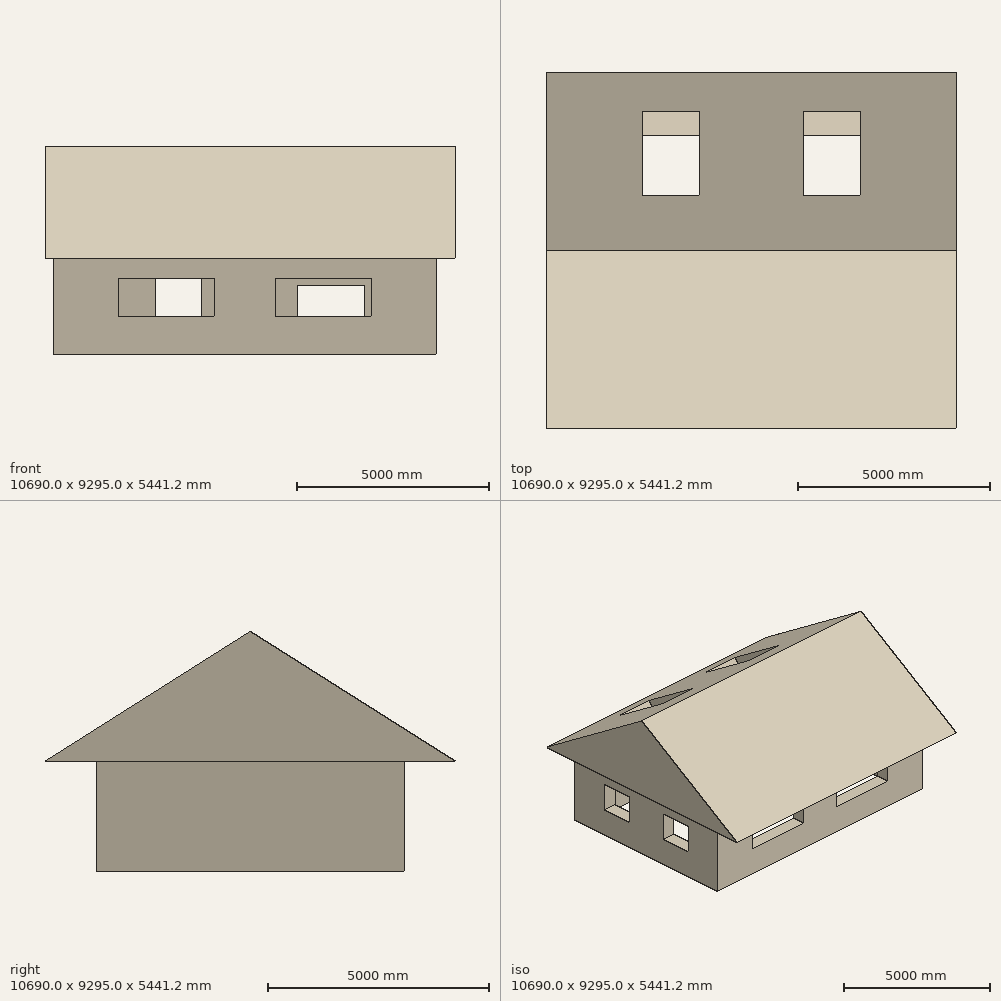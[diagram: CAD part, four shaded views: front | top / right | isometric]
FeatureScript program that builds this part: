
annotation { "Feature Type Name" : "Feature", "Feature Type Description" : "" }
export const myFeature = defineFeature(function(context is Context, id is Id, definition is map)
    precondition{}
    {
        {
            var Q0;
            Q0=qCreatedBy(makeId("Top.planeOp"),FACE);
            var sketch = newSketch(context, id + "F0", { "sketchPlane" : qUnion([Q0])});
            skLineSegment(sketch, "E0.bottom", {"start": v(-4999.87, 2448.69) * mm, "end": v(5000.13, 2448.69) * mm});
            skLineSegment(sketch, "E0.top", {"start": v(-4999.87, -4551.31) * mm, "end": v(5000.13, -4551.31) * mm});
            skLineSegment(sketch, "E0.left", {"start": v(-4999.87, 2448.69) * mm, "end": v(-4999.87, -4551.31) * mm});
            skLineSegment(sketch, "E0.right", {"start": v(5000.13, 2448.69) * mm, "end": v(5000.13, -4551.31) * mm});
            skLineSegment(sketch, "E1.bottom", {"start": v(-4499.87, 1948.69) * mm, "end": v(4500.13, 1948.69) * mm});
            skLineSegment(sketch, "E1.top", {"start": v(-4499.87, -4051.31) * mm, "end": v(4500.13, -4051.31) * mm});
            skLineSegment(sketch, "E1.left", {"start": v(-4499.87, 1948.69) * mm, "end": v(-4499.87, -4051.31) * mm});
            skLineSegment(sketch, "E1.right", {"start": v(4500.13, 1948.69) * mm, "end": v(4500.13, -4051.31) * mm});
            skLineSegment(sketch, "E2.0", {"start": v(-4999.87, 2443.69) * mm, "end": v(5000.13, 2443.69) * mm});
            skLineSegment(sketch, "E3.bottom", {"start": v(-2859.87, 2443.69) * mm, "end": v(-1609.87, 2443.69) * mm});
            skLineSegment(sketch, "E3.top", {"start": v(-2859.87, 1948.69) * mm, "end": v(-1609.87, 1948.69) * mm});
            skLineSegment(sketch, "E3.left", {"start": v(-2859.87, 2443.69) * mm, "end": v(-2859.87, 1948.69) * mm});
            skLineSegment(sketch, "E3.right", {"start": v(-1609.87, 2443.69) * mm, "end": v(-1609.87, 1948.69) * mm});
            skLineSegment(sketch, "E4.bottom", {"start": v(1610.13, 2443.69) * mm, "end": v(2860.13, 2443.69) * mm});
            skLineSegment(sketch, "E4.top", {"start": v(1610.13, 1948.69) * mm, "end": v(2860.13, 1948.69) * mm});
            skLineSegment(sketch, "E4.left", {"start": v(1610.13, 2443.69) * mm, "end": v(1610.13, 1948.69) * mm});
            skLineSegment(sketch, "E4.right", {"start": v(2860.13, 2443.69) * mm, "end": v(2860.13, 1948.69) * mm});
            skLineSegment(sketch, "E5.bottom", {"start": v(4500.13, 198.69) * mm, "end": v(5000.13, 198.69) * mm});
            skLineSegment(sketch, "E5.top", {"start": v(4500.13, -1051.31) * mm, "end": v(5000.13, -1051.31) * mm});
            skLineSegment(sketch, "E5.left", {"start": v(4500.13, 198.69) * mm, "end": v(4500.13, -1051.31) * mm});
            skLineSegment(sketch, "E5.right", {"start": v(5000.13, 198.69) * mm, "end": v(5000.13, -1051.31) * mm});
            skLineSegment(sketch, "E6.bottom", {"start": v(4500.13, -2032.66) * mm, "end": v(5000.13, -2032.66) * mm});
            skLineSegment(sketch, "E6.top", {"start": v(4500.13, -3239.36) * mm, "end": v(5000.13, -3239.36) * mm});
            skLineSegment(sketch, "E6.left", {"start": v(4500.13, -2032.66) * mm, "end": v(4500.13, -3239.36) * mm});
            skLineSegment(sketch, "E6.right", {"start": v(5000.13, -2032.66) * mm, "end": v(5000.13, -3239.36) * mm});
            skLineSegment(sketch, "E7.bottom", {"start": v(-4999.87, 303.69) * mm, "end": v(-4499.87, 303.69) * mm});
            skLineSegment(sketch, "E7.top", {"start": v(-4999.87, 0) * mm, "end": v(-4499.87, 0) * mm});
            skLineSegment(sketch, "E7.left", {"start": v(-4999.87, 303.69) * mm, "end": v(-4999.87, 0) * mm});
            skLineSegment(sketch, "E7.right", {"start": v(-4499.87, 303.69) * mm, "end": v(-4499.87, 0) * mm});
            skLineSegment(sketch, "E8.bottom", {"start": v(-4999.87, -1051.31) * mm, "end": v(-4499.87, -1051.31) * mm});
            skLineSegment(sketch, "E8.top", {"start": v(-4999.87, -2411.31) * mm, "end": v(-4499.87, -2411.31) * mm});
            skLineSegment(sketch, "E8.left", {"start": v(-4999.87, -1051.31) * mm, "end": v(-4999.87, -2411.31) * mm});
            skLineSegment(sketch, "E8.right", {"start": v(-4499.87, -1051.31) * mm, "end": v(-4499.87, -2411.31) * mm});
            skLineSegment(sketch, "E9.bottom", {"start": v(-2859.87, -4051.31) * mm, "end": v(-1609.87, -4051.31) * mm});
            skLineSegment(sketch, "E9.top", {"start": v(-2859.87, -4551.31) * mm, "end": v(-1609.87, -4551.31) * mm});
            skLineSegment(sketch, "E9.left", {"start": v(-2859.87, -4051.31) * mm, "end": v(-2859.87, -4551.31) * mm});
            skLineSegment(sketch, "E9.right", {"start": v(-1609.87, -4051.31) * mm, "end": v(-1609.87, -4551.31) * mm});
            skLineSegment(sketch, "E10.bottom", {"start": v(1610.13, -4051.31) * mm, "end": v(2860.13, -4051.31) * mm});
            skLineSegment(sketch, "E10.top", {"start": v(1610.13, -4551.31) * mm, "end": v(2860.13, -4551.31) * mm});
            skLineSegment(sketch, "E10.left", {"start": v(1610.13, -4051.31) * mm, "end": v(1610.13, -4551.31) * mm});
            skLineSegment(sketch, "E10.right", {"start": v(2860.13, -4051.31) * mm, "end": v(2860.13, -4551.31) * mm});
            skSolve(sketch);
        }
        {
            var Q0;
            {var subQ3=sQuery(id+"F0.wireOp",EDGE,"E3.left");Q0=makeQuery(id+"F0.imprint","IMPRINT",FACE,{"disambiguationData":[TD([[makeQuery(id+"F0.imprint","IMPRINT",EDGE,{"derivedFrom":subQ3}),-1.0]])]});}
            var Q1;
            {var subQ2=sQuery(id+"F0.wireOp",EDGE,"E3.left");Q1=makeQuery(id+"F0.imprint","IMPRINT",FACE,{"disambiguationData":[TD([[makeQuery(id+"F0.imprint","IMPRINT",EDGE,{"derivedFrom":subQ2}),1.0]])]});}
            var Q2;
            {var subQ0=sQuery(id+"F0.wireOp",EDGE,"E3.right");Q2=makeQuery(id+"F0.imprint","IMPRINT",FACE,{"disambiguationData":[TD([[makeQuery(id+"F0.imprint","IMPRINT",EDGE,{"derivedFrom":subQ0}),1.0]])]});}
            var Q3;
            {var subQ2=sQuery(id+"F0.wireOp",EDGE,"E4.left");Q3=makeQuery(id+"F0.imprint","IMPRINT",FACE,{"disambiguationData":[TD([[makeQuery(id+"F0.imprint","IMPRINT",EDGE,{"derivedFrom":subQ2}),1.0]])]});}
            var Q4;
            {var subQ3=sQuery(id+"F0.wireOp",EDGE,"E4.right");Q4=makeQuery(id+"F0.imprint","IMPRINT",FACE,{"disambiguationData":[TD([[makeQuery(id+"F0.imprint","IMPRINT",EDGE,{"derivedFrom":subQ3}),1.0]])]});}
            var Q5;
            {var subQ0=sQuery(id+"F0.wireOp",EDGE,"E5.bottom");Q5=makeQuery(id+"F0.imprint","IMPRINT",FACE,{"disambiguationData":[TD([[makeQuery(id+"F0.imprint","IMPRINT",EDGE,{"derivedFrom":subQ0}),-1.0]])]});}
            var Q6;
            {var subQ0=sQuery(id+"F0.wireOp",EDGE,"E6.bottom");Q6=makeQuery(id+"F0.imprint","IMPRINT",FACE,{"disambiguationData":[TD([[makeQuery(id+"F0.imprint","IMPRINT",EDGE,{"derivedFrom":subQ0}),-1.0]])]});}
            var Q7;
            {var subQ0=sQuery(id+"F0.wireOp",EDGE,"E5.top");Q7=makeQuery(id+"F0.imprint","IMPRINT",FACE,{"disambiguationData":[TD([[makeQuery(id+"F0.imprint","IMPRINT",EDGE,{"derivedFrom":subQ0}),-1.0]])]});}
            var Q8;
            {var subQ3=sQuery(id+"F0.wireOp",EDGE,"E6.top");Q8=makeQuery(id+"F0.imprint","IMPRINT",FACE,{"disambiguationData":[TD([[makeQuery(id+"F0.imprint","IMPRINT",EDGE,{"derivedFrom":subQ3}),-1.0]])]});}
            var Q9;
            {var subQ2=sQuery(id+"F0.wireOp",EDGE,"E10.left");Q9=makeQuery(id+"F0.imprint","IMPRINT",FACE,{"disambiguationData":[TD([[makeQuery(id+"F0.imprint","IMPRINT",EDGE,{"derivedFrom":subQ2}),1.0]])]});}
            var Q10;
            {var subQ0=sQuery(id+"F0.wireOp",EDGE,"E9.right");Q10=makeQuery(id+"F0.imprint","IMPRINT",FACE,{"disambiguationData":[TD([[makeQuery(id+"F0.imprint","IMPRINT",EDGE,{"derivedFrom":subQ0}),1.0]])]});}
            var Q11;
            {var subQ2=sQuery(id+"F0.wireOp",EDGE,"E9.left");Q11=makeQuery(id+"F0.imprint","IMPRINT",FACE,{"disambiguationData":[TD([[makeQuery(id+"F0.imprint","IMPRINT",EDGE,{"derivedFrom":subQ2}),1.0]])]});}
            var Q12;
            {var subQ0=sQuery(id+"F0.wireOp",EDGE,"E8.top");Q12=makeQuery(id+"F0.imprint","IMPRINT",FACE,{"disambiguationData":[TD([[makeQuery(id+"F0.imprint","IMPRINT",EDGE,{"derivedFrom":subQ0}),-1.0]])]});}
            var Q13;
            {var subQ0=sQuery(id+"F0.wireOp",EDGE,"E8.bottom");Q13=makeQuery(id+"F0.imprint","IMPRINT",FACE,{"disambiguationData":[TD([[makeQuery(id+"F0.imprint","IMPRINT",EDGE,{"derivedFrom":subQ0}),-1.0]])]});}
            var Q14;
            {var subQ0=sQuery(id+"F0.wireOp",EDGE,"E7.top");Q14=makeQuery(id+"F0.imprint","IMPRINT",FACE,{"disambiguationData":[TD([[makeQuery(id+"F0.imprint","IMPRINT",EDGE,{"derivedFrom":subQ0}),-1.0]])]});}
            var Q15;
            {var subQ0=sQuery(id+"F0.wireOp",EDGE,"E7.bottom");Q15=makeQuery(id+"F0.imprint","IMPRINT",FACE,{"disambiguationData":[TD([[makeQuery(id+"F0.imprint","IMPRINT",EDGE,{"derivedFrom":subQ0}),-1.0]])]});}
            extrude(context, id + "F1", {"entities" : qUnion([Q0, Q1, Q2, Q3, Q4, Q5, Q6, Q7, Q8, Q9, Q10, Q11, Q12, Q13, Q14, Q15]), "depth" : 2500 * mm, "offsetDistance" : 25 * mm});
        }
        {
            var Q0;
            Q0=makeQuery(id+"F1.opExtrude","SWEPT_FACE",FACE,{"disambiguationData":[OSD([sQuery(id+"F0.wireOp",EDGE,"E2.0")])]});
            var sketch = newSketch(context, id + "F2", { "sketchPlane" : qUnion([Q0])});
            skLineSegment(sketch, "E11.bottom", {"start": v(-3127.73, 1800) * mm, "end": v(-1357.73, 1800) * mm});
            skLineSegment(sketch, "E11.top", {"start": v(-3127.73, 0) * mm, "end": v(-1357.73, 0) * mm});
            skLineSegment(sketch, "E11.left", {"start": v(-3127.73, 1800) * mm, "end": v(-3127.73, 0) * mm});
            skLineSegment(sketch, "E11.right", {"start": v(-1357.73, 1800) * mm, "end": v(-1357.73, 0) * mm});
            skLineSegment(sketch, "E12.bottom", {"start": v(1129.3, 2000) * mm, "end": v(2329.3, 2000) * mm});
            skLineSegment(sketch, "E12.top", {"start": v(1129.3, 1000) * mm, "end": v(2329.3, 1000) * mm});
            skLineSegment(sketch, "E12.left", {"start": v(1129.3, 2000) * mm, "end": v(1129.3, 1000) * mm});
            skLineSegment(sketch, "E12.right", {"start": v(2329.3, 2000) * mm, "end": v(2329.3, 1000) * mm});
            skSolve(sketch);
        }
        {
            var Q0;
            Q0=makeQuery(id+"F2.imprint","IMPRINT",FACE,{"disambiguationData":[TD([[makeQuery(id+"F2.imprint","IMPRINT",EDGE,{"derivedFrom":sQuery(id+"F2.wireOp",EDGE,"E11.bottom")}),-1.0]])]});
            var Q1;
            Q1=makeQuery(id+"F2.imprint","IMPRINT",FACE,{"disambiguationData":[TD([[makeQuery(id+"F2.imprint","IMPRINT",EDGE,{"derivedFrom":sQuery(id+"F2.wireOp",EDGE,"E12.bottom")}),-1.0]])]});
            extrude(context, id + "F3", {"entities" : qUnion([Q0, Q1]), "operationType" : NewBodyOperationType.REMOVE, "endBound" : BoundingType.UP_TO_NEXT, "oppositeDirection" : true, "depth" : 25 * mm, "offsetDistance" : 25 * mm});
        }
        {
            var Q0;
            Q0=makeQuery(id+"F1.opExtrude","SWEPT_FACE",FACE,{"disambiguationData":[OSD([sQuery(id+"F0.wireOp",EDGE,"E0.left")])]});
            var sketch = newSketch(context, id + "F4", { "sketchPlane" : qUnion([Q0])});
            skLineSegment(sketch, "E13.bottom", {"start": v(-953.72, 2000) * mm, "end": v(246.28, 2000) * mm});
            skLineSegment(sketch, "E13.top", {"start": v(-953.72, 1000) * mm, "end": v(246.28, 1000) * mm});
            skLineSegment(sketch, "E13.left", {"start": v(-953.72, 2000) * mm, "end": v(-953.72, 1000) * mm});
            skLineSegment(sketch, "E13.right", {"start": v(246.28, 2000) * mm, "end": v(246.28, 1000) * mm});
            skLineSegment(sketch, "E14.bottom", {"start": v(1918.9, 2000) * mm, "end": v(3118.9, 2000) * mm});
            skLineSegment(sketch, "E14.top", {"start": v(1918.9, 1000) * mm, "end": v(3118.9, 1000) * mm});
            skLineSegment(sketch, "E14.left", {"start": v(1918.9, 2000) * mm, "end": v(1918.9, 1000) * mm});
            skLineSegment(sketch, "E14.right", {"start": v(3118.9, 2000) * mm, "end": v(3118.9, 1000) * mm});
            skSolve(sketch);
        }
        {
            var Q0;
            Q0=makeQuery(id+"F4.imprint","IMPRINT",FACE,{"disambiguationData":[TD([[makeQuery(id+"F4.imprint","IMPRINT",EDGE,{"derivedFrom":sQuery(id+"F4.wireOp",EDGE,"E13.bottom")}),-1.0]])]});
            var Q1;
            Q1=makeQuery(id+"F4.imprint","IMPRINT",FACE,{"disambiguationData":[TD([[makeQuery(id+"F4.imprint","IMPRINT",EDGE,{"derivedFrom":sQuery(id+"F4.wireOp",EDGE,"E14.bottom")}),-1.0]])]});
            extrude(context, id + "F5", {"entities" : qUnion([Q0, Q1]), "operationType" : NewBodyOperationType.REMOVE, "endBound" : BoundingType.UP_TO_NEXT, "oppositeDirection" : true, "depth" : 25 * mm, "offsetDistance" : 25 * mm});
        }
        {
            var Q0;
            Q0=makeQuery(id+"F1.opExtrude","SWEPT_FACE",FACE,{"disambiguationData":[OSD([sQuery(id+"F0.wireOp",EDGE,"E0.right")])]});
            var sketch = newSketch(context, id + "F6", { "sketchPlane" : qUnion([Q0])});
            skLineSegment(sketch, "E15", {"start": v(2443.69, 2500) * mm, "end": v(-4551.31, 2500) * mm});
            skLineSegment(sketch, "E16", {"start": v(-4551.31, 2500) * mm, "end": v(-5701.31, 2500) * mm});
            skLineSegment(sketch, "E17", {"start": v(-5701.31, 2500) * mm, "end": v(-1053.81, 5441.21) * mm});
            skLineSegment(sketch, "E18", {"start": v(-1053.81, 5441.21) * mm, "end": v(3593.69, 2500) * mm});
            skLineSegment(sketch, "E19", {"start": v(3593.69, 2500) * mm, "end": v(-5701.31, 2500) * mm});
            skLineSegment(sketch, "E20", {"start": v(-5701.31, 2500) * mm, "end": v(-5701.31, 0) * mm});
            skLineSegment(sketch, "E21", {"start": v(3593.69, 2500) * mm, "end": v(3593.69, 0) * mm});
            skLineSegment(sketch, "E22", {"start": v(3593.69, 0) * mm, "end": v(-5701.31, 0) * mm});
            skSolve(sketch);
        }
        {
            var Q0;
            {var subQ5=sQuery(id+"F6.wireOp",EDGE,"E17");Q0=makeQuery(id+"F6.imprint","IMPRINT",FACE,{"disambiguationData":[TD([[makeQuery(id+"F6.imprint","IMPRINT",EDGE,{"derivedFrom":subQ5}),-1.0]])]});}
            extrude(context, id + "F7", {"entities" : qUnion([Q0]), "operationType" : NewBodyOperationType.ADD, "oppositeDirection" : true, "depth" : 10200 * mm, "offsetDistance" : 25 * mm, "hasSecondDirection" : true, "secondDirectionOppositeDirection" : false, "secondDirectionDepth" : 490 * mm});
        }
        {
            var Q0;
            Q0=makeQuery(id+"F1.opExtrude","SWEPT_FACE",FACE,{"disambiguationData":[OSD([sQuery(id+"F0.wireOp",EDGE,"E0.top")])]});
            var sketch = newSketch(context, id + "F8", { "sketchPlane" : qUnion([Q0])});
            skLineSegment(sketch, "E23.bottom", {"start": v(-3299.87, 2000) * mm, "end": v(-799.87, 2000) * mm});
            skLineSegment(sketch, "E23.top", {"start": v(-3299.87, 1000) * mm, "end": v(-799.87, 1000) * mm});
            skLineSegment(sketch, "E23.left", {"start": v(-3299.87, 2000) * mm, "end": v(-3299.87, 1000) * mm});
            skLineSegment(sketch, "E23.right", {"start": v(-799.87, 2000) * mm, "end": v(-799.87, 1000) * mm});
            skLineSegment(sketch, "E24.bottom", {"start": v(800.13, 2000) * mm, "end": v(3300.13, 2000) * mm});
            skLineSegment(sketch, "E24.top", {"start": v(800.13, 1000) * mm, "end": v(3300.13, 1000) * mm});
            skLineSegment(sketch, "E24.left", {"start": v(800.13, 2000) * mm, "end": v(800.13, 1000) * mm});
            skLineSegment(sketch, "E24.right", {"start": v(3300.13, 2000) * mm, "end": v(3300.13, 1000) * mm});
            skSolve(sketch);
        }
        {
            var Q0;
            Q0=makeQuery(id+"F8.imprint","IMPRINT",FACE,{"disambiguationData":[TD([[makeQuery(id+"F8.imprint","IMPRINT",EDGE,{"derivedFrom":sQuery(id+"F8.wireOp",EDGE,"E23.bottom")}),-1.0]])]});
            var Q1;
            Q1=makeQuery(id+"F8.imprint","IMPRINT",FACE,{"disambiguationData":[TD([[makeQuery(id+"F8.imprint","IMPRINT",EDGE,{"derivedFrom":sQuery(id+"F8.wireOp",EDGE,"E24.bottom")}),-1.0]])]});
            extrude(context, id + "F9", {"entities" : qUnion([Q0, Q1]), "operationType" : NewBodyOperationType.REMOVE, "endBound" : BoundingType.UP_TO_NEXT, "oppositeDirection" : true, "depth" : 25 * mm, "offsetDistance" : 25 * mm});
        }
        {
            var Q0;
            Q0=makeQuery(id+"F7.opExtrude","SWEPT_FACE",FACE,{"disambiguationData":[OSD([sQuery(id+"F6.wireOp",EDGE,"E18")])]});
            var sketch = newSketch(context, id + "F10", { "sketchPlane" : qUnion([Q0])});
            skLineSegment(sketch, "E25.bottom", {"start": v(2990.13, -2100.25) * mm, "end": v(1490.13, -2100.25) * mm});
            skLineSegment(sketch, "E25.top", {"start": v(2990.13, 499.75) * mm, "end": v(1490.13, 499.75) * mm});
            skLineSegment(sketch, "E25.left", {"start": v(2990.13, -2100.25) * mm, "end": v(2990.13, 499.75) * mm});
            skLineSegment(sketch, "E25.right", {"start": v(1490.13, -2100.25) * mm, "end": v(1490.13, 499.75) * mm});
            skLineSegment(sketch, "E26.bottom", {"start": v(-1199.87, -2100.25) * mm, "end": v(-2699.87, -2100.25) * mm});
            skLineSegment(sketch, "E26.top", {"start": v(-1199.87, 499.75) * mm, "end": v(-2699.87, 499.75) * mm});
            skLineSegment(sketch, "E26.left", {"start": v(-1199.87, -2100.25) * mm, "end": v(-1199.87, 499.75) * mm});
            skLineSegment(sketch, "E26.right", {"start": v(-2699.87, -2100.25) * mm, "end": v(-2699.87, 499.75) * mm});
            skSolve(sketch);
        }
        {
            var Q0;
            Q0=makeQuery(id+"F10.imprint","IMPRINT",FACE,{"disambiguationData":[TD([[makeQuery(id+"F10.imprint","IMPRINT",EDGE,{"derivedFrom":sQuery(id+"F10.wireOp",EDGE,"E25.bottom")}),-1.0]])]});
            var Q1;
            Q1=makeQuery(id+"F10.imprint","IMPRINT",FACE,{"disambiguationData":[TD([[makeQuery(id+"F10.imprint","IMPRINT",EDGE,{"derivedFrom":sQuery(id+"F10.wireOp",EDGE,"E26.bottom")}),-1.0]])]});
            extrude(context, id + "F11", {"entities" : qUnion([Q0, Q1]), "operationType" : NewBodyOperationType.REMOVE, "endBound" : BoundingType.UP_TO_NEXT, "oppositeDirection" : true, "depth" : 25 * mm, "offsetDistance" : 25 * mm});
        }
    });
